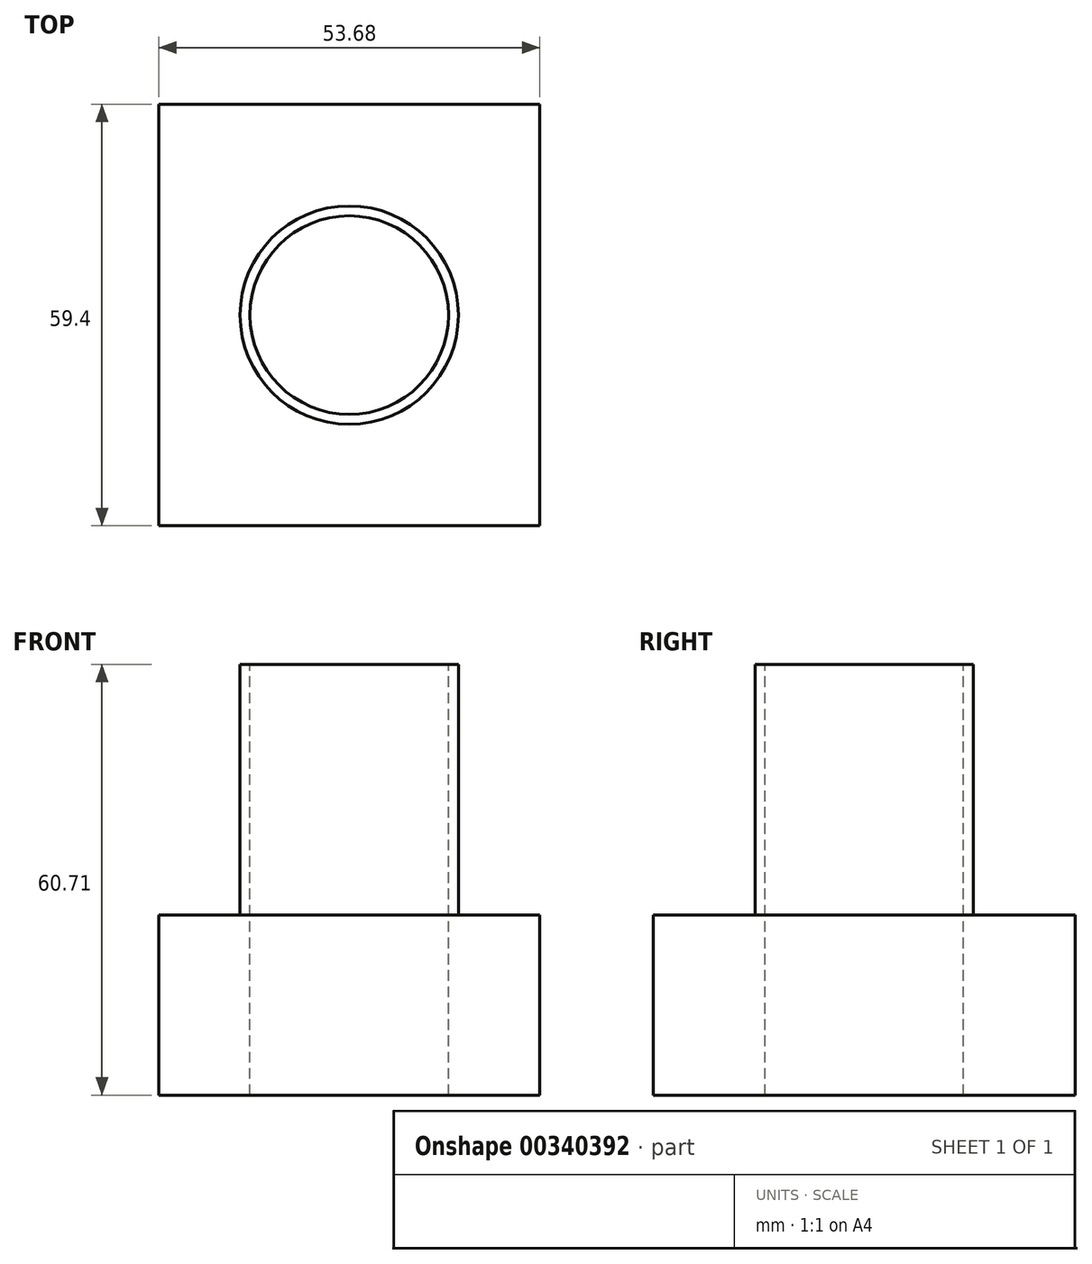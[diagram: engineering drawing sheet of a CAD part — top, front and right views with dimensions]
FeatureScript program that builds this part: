
annotation { "Feature Type Name" : "Feature", "Feature Type Description" : "" }
export const myFeature = defineFeature(function(context is Context, id is Id, definition is map)
    precondition{}
    {
        {
            var Q0;
            Q0=qCreatedBy(makeId("Top.planeOp"),FACE);
            var sketch = newSketch(context, id + "F0", { "sketchPlane" : qUnion([Q0])});
            skLineSegment(sketch, "E0.bottom", {"start": v(-26.84, -29.7) * mm, "end": v(26.84, -29.7) * mm});
            skLineSegment(sketch, "E0.top", {"start": v(-26.84, 29.7) * mm, "end": v(26.84, 29.7) * mm});
            skLineSegment(sketch, "E0.left", {"start": v(-26.84, -29.7) * mm, "end": v(-26.84, 29.7) * mm});
            skLineSegment(sketch, "E0.right", {"start": v(26.84, -29.7) * mm, "end": v(26.84, 29.7) * mm});
            skPoint(sketch, "E0.middle", {"position": v(0, 0) * mm});
            skSolve(sketch);
        }
        {
            var Q0;
            Q0=makeQuery(id+"F0.imprint","IMPRINT",FACE,{"disambiguationData":[TD([[makeQuery(id+"F0.imprint","IMPRINT",EDGE,{"derivedFrom":sQuery(id+"F0.wireOp",EDGE,"E0.bottom")}),1.0]])]});
            var sketch = newSketch(context, id + "F1", { "sketchPlane" : qUnion([Q0])});
            skCircle(sketch, "E1", {"center": v(0, 0) * mm, "radius": 15.38 * mm});
            skSolve(sketch);
        }
        {
            var Q0;
            Q0=makeQuery(id+"F1.imprint","IMPRINT",FACE,{"disambiguationData":[TD([[makeQuery(id+"F1.imprint","IMPRINT",EDGE,{"derivedFrom":sQuery(id+"F1.wireOp",EDGE,"E1")}),-1.0]])]});
            extrude(context, id + "F2", {"entities" : qUnion([Q0]), "depth" : 25.4 * mm});
        }
        {
            var Q0;
            Q0=makeQuery(id+"F1.imprint","IMPRINT",FACE,{"disambiguationData":[TD([[makeQuery(id+"F1.imprint","IMPRINT",EDGE,{"derivedFrom":sQuery(id+"F1.wireOp",EDGE,"E1")}),1.0]])]});
            extrude(context, id + "F3", {"entities" : qUnion([Q0]), "operationType" : NewBodyOperationType.ADD, "depth" : 60.7 * mm});
        }
        {
            var Q0;
            Q0=makeQuery(id+"F3.opExtrude","CAP_FACE",FACE,{"disambiguationData":[OSD([sQuery(id+"F1.wireOp",EDGE,"E1")])],"isStart":false});
            var sketch = newSketch(context, id + "F4", { "sketchPlane" : qUnion([Q0])});
            skCircle(sketch, "E2", {"center": v(0, 0) * mm, "radius": 13.99 * mm});
            skSolve(sketch);
        }
        {
            var Q0;
            Q0=makeQuery(id+"F4.imprint","IMPRINT",FACE,{"disambiguationData":[TD([[makeQuery(id+"F4.imprint","IMPRINT",EDGE,{"derivedFrom":sQuery(id+"F4.wireOp",EDGE,"E2")}),1.0]])]});
            extrude(context, id + "F5", {"entities" : qUnion([Q0]), "operationType" : NewBodyOperationType.REMOVE, "oppositeDirection" : true, "depth" : 95.25 * mm});
        }
    });
